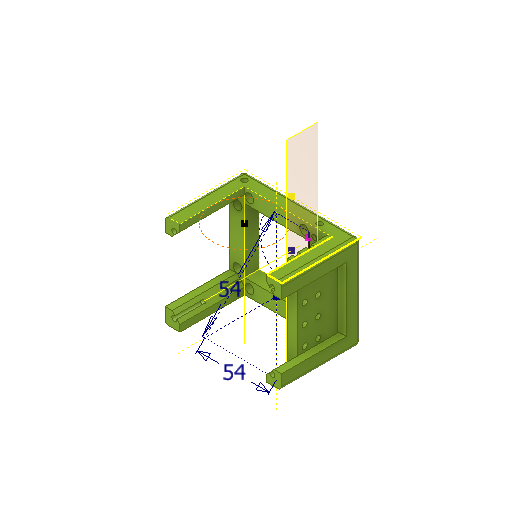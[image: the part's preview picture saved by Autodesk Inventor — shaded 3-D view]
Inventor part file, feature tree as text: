
AUTODESK INVENTOR PART (.ipt)
format: ipt  version: 2022 (Build 260153000, 153)  size: 473,088 bytes
history: native  units: mm
features: sketch x13, projected_geometry x12, hole x6, other x5, extrude x4, plane x2, reference x2, fillet x1
ambient origin geometry x8: Origin, YZ Plane, XZ Plane, XY Plane, X Axis, Y Axis, Z Axis, Center Point
bodies: Solid1 (feature_tree)
feature tree (45):
  extrude  "Extrusion1"  Depth=49.8mm
  extrude  "Extrusion2"  Depth=7.7mm TaperAngle=0.0deg
  hole  "Hole1"  [1 undecoded]
  sketch  "Sketch4"  dims[d8=2.8mm d9=6.0mm d10=5.5mm d11=3.1mm d12=90.0deg d13=16.0mm d14=20.594885mm d23=2.0mm d30=33.8mm d31=0.0mm]
  sketch  "Sketch5"  dims[d42=2.8mm d43=6.0mm d44=3.0mm d45=2.0mm d46=90.0deg d47=15.0mm d48=20.594885mm]
  other  "Work Axis1"
  other  "Work Axis2"
  fillet  "Fillet1"  Radius=33.8mm
  extrude  "Extrusion3"  Depth=4.9mm
  sketch  "Sketch8"  dims[d74=2.9mm d75=6.0mm d76=4.0mm d77=2.0mm d78=90.0deg d79=6.5mm d80=20.594885mm]
  plane  "Work Plane1"
  hole  "Hole2"  [1 undecoded]
  hole  "Hole5"  [1 undecoded]
  hole  "Hole6"  [1 undecoded]
  hole  "Hole7"  [1 undecoded]
  hole  "Hole8"  [1 undecoded]
  plane  "Arbeitsebene4"
  extrude  "Extrusion6"  Depth=10.0mm
  sketch  "Sketch1"  dims[d0=49.8mm d1=49.8mm]
  sketch  "Sketch2"  dims[d2=7.85mm d3=7.7mm d4=0.0mm]
  projected_geometry  "Projected Loop1"
  sketch  "Sketch3"  dims[d5=34.4mm d6=0.0mm]
  projected_geometry  "Projected Loop3"
  sketch  "Sketch6"  dims[d67=2.9mm d68=6.0mm d69=4.0mm d70=2.0mm d71=90.0deg d72=6.5mm d73=20.594885mm]
  projected_geometry  "Projected Loop4"
  projected_geometry  "Projected Loop5"
  projected_geometry  "Projected Loop6"
  projected_geometry  "Projected Loop7"
  sketch  "Sketch9"  dims[d81=2.9mm d82=6.0mm d83=4.0mm d84=2.0mm d85=90.0deg d86=6.5mm d87=20.594885mm d91=4.9mm]
  sketch  "Sketch12"  dims[d92=4.9mm d93=4.9mm]
  sketch  "Sketch13"  dims[d94=4.9mm d96=4.9mm]
  sketch  "Sketch14"  dims[d97=4.9mm d98=4.9mm]
  sketch  "Sketch15"  dims[d99=4.9mm d100=4.9mm]
  projected_geometry  "Projected Loop13"
  projected_geometry  "Projected Loop14"
  projected_geometry  "Projizierte Kontur16"
  projected_geometry  "Projizierte Kontur17"
  projected_geometry  "Projizierte Kontur18"
  projected_geometry  "Projizierte Kontur19"
  sketch  "Skizze17"  dims[d101=4.9mm d111=0.0mm d113=4.7mm d114=6.0mm d115=4.0mm d116=2.0mm d117=90.0deg d118=8.0mm d119=20.594885mm d120=54.2mm d121=54.2mm d122=54.0mm d123=54.0mm d124=12.0mm d125=7.85mm d126=2.8mm d127=2.8mm d128=2.8mm d129=2.8mm d130=30.0mm d132=10.0mm d133=40.0mm d135=10.0mm d138=5.0mm d139=0.0mm d140=4.9mm d141=4.9mm]
  reference  "Referenz5"
  reference  "Referenz6"
  other  "Baugruppe1"
  other  "Assebmly_Linear_Stepper_90mm:1"
  other  "00_Linear_Stepper_90mm:1"
note: 6 required parameter values undecoded (feature->parameter linkage not recoverable at this tier; creation-order binding heuristic only, values carry confidence <= 0.55)
